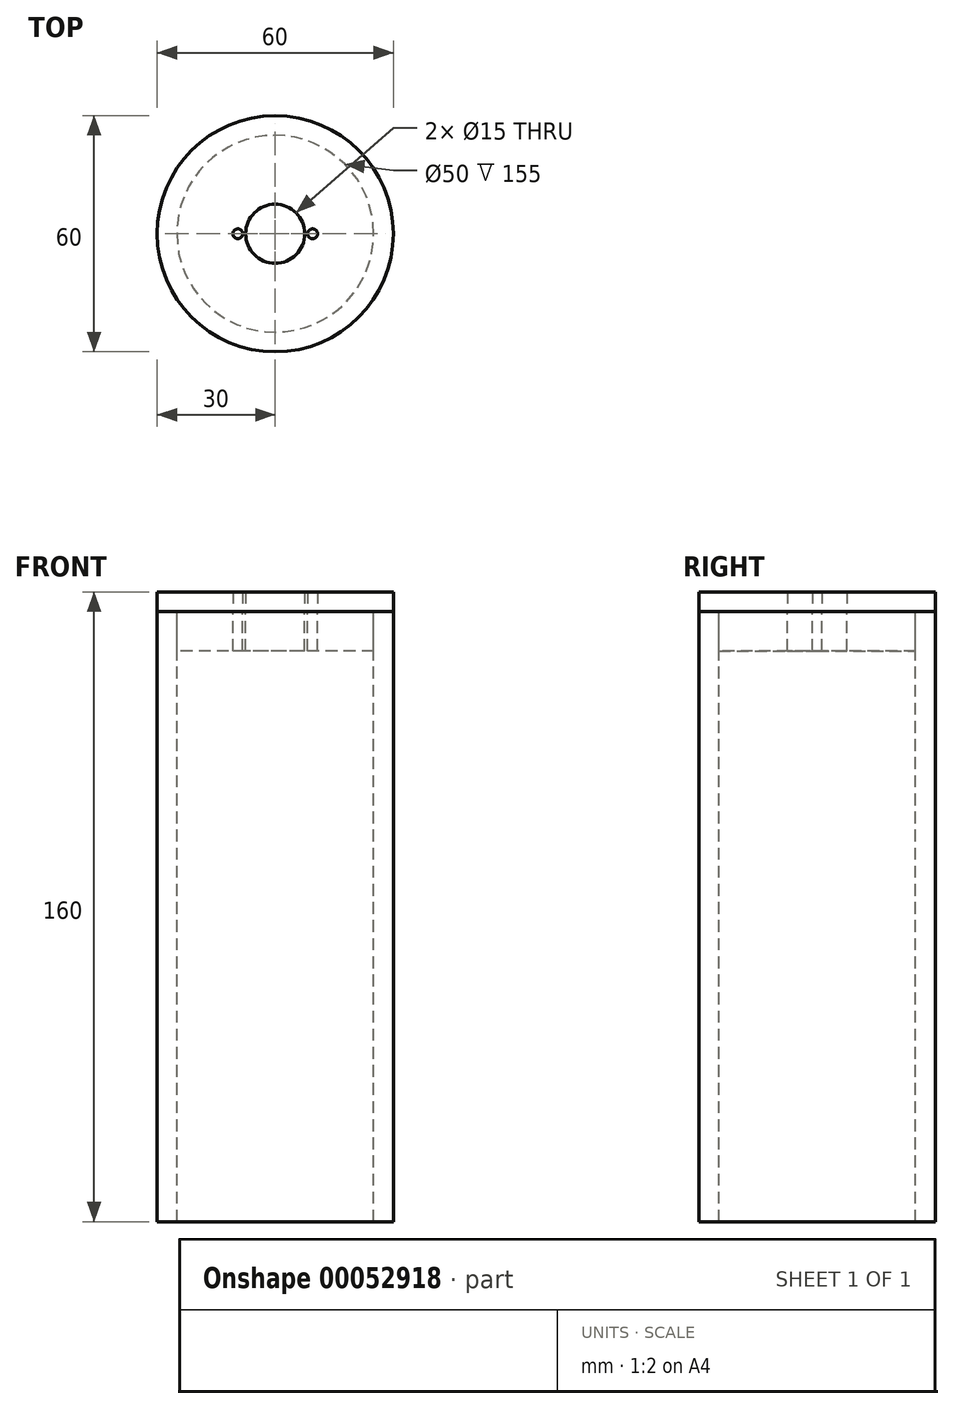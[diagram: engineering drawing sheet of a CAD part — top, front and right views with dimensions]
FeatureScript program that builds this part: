
annotation { "Feature Type Name" : "Feature", "Feature Type Description" : "" }
export const myFeature = defineFeature(function(context is Context, id is Id, definition is map)
    precondition{}
    {
        {
            var Q0;
            Q0=qCreatedBy(makeId("Top.planeOp"),FACE);
            var sketch = newSketch(context, id + "F0", { "sketchPlane" : qUnion([Q0])});
            skCircle(sketch, "E0", {"center": v(0, 0) * mm, "radius": 30 * mm});
            skCircle(sketch, "E1", {"center": v(0, 0) * mm, "radius": 25 * mm});
            skCircle(sketch, "E2", {"center": v(0, 0) * mm, "radius": 7.5 * mm});
            skCircle(sketch, "E3", {"center": v(9.5, 0) * mm, "radius": 1.25 * mm});
            skCircle(sketch, "E4", {"center": v(-9.5, 0) * mm, "radius": 1.25 * mm});
            skSolve(sketch);
        }
        {
            var Q0;
            Q0=makeQuery(id+"F0.imprint","IMPRINT",FACE,{"disambiguationData":[TD([[makeQuery(id+"F0.imprint","IMPRINT",EDGE,{"derivedFrom":sQuery(id+"F0.wireOp",EDGE,"E0")}),1.0]])]});
            extrude(context, id + "F1", {"entities" : qUnion([Q0]), "oppositeDirection" : true, "depth" : 155 * mm});
        }
        {
            var Q0;
            Q0=makeQuery(id+"F0.imprint","IMPRINT",FACE,{"disambiguationData":[TD([[makeQuery(id+"F0.imprint","IMPRINT",EDGE,{"derivedFrom":sQuery(id+"F0.wireOp",EDGE,"E1")}),1.0]])]});
            extrude(context, id + "F2", {"entities" : qUnion([Q0]), "oppositeDirection" : true, "depth" : 10 * mm});
        }
        {
            var Q0;
            Q0=makeQuery(id+"F0.imprint","IMPRINT",FACE,{"disambiguationData":[TD([[makeQuery(id+"F0.imprint","IMPRINT",EDGE,{"derivedFrom":sQuery(id+"F0.wireOp",EDGE,"E1")}),1.0]])]});
            var Q1;
            Q1=makeQuery(id+"F0.imprint","IMPRINT",FACE,{"disambiguationData":[TD([[makeQuery(id+"F0.imprint","IMPRINT",EDGE,{"derivedFrom":sQuery(id+"F0.wireOp",EDGE,"E0")}),1.0]])]});
            extrude(context, id + "F3", {"entities" : qUnion([Q0, Q1]), "depth" : 5 * mm});
        }
    });
